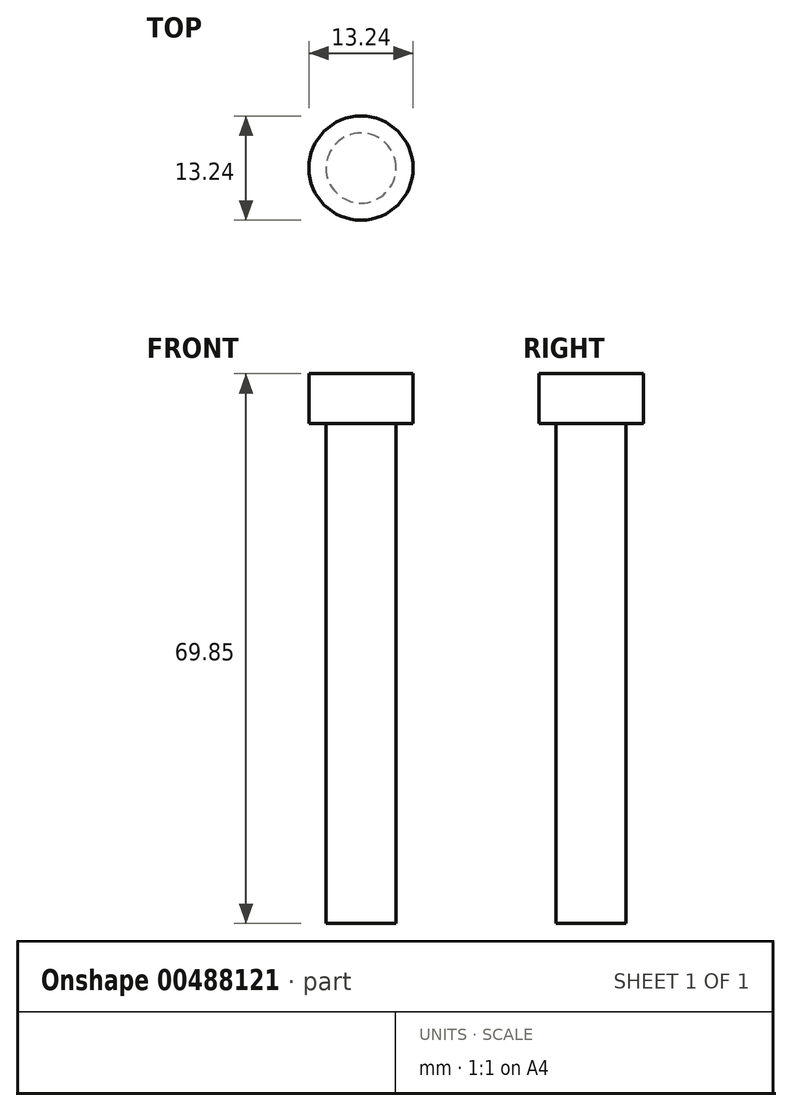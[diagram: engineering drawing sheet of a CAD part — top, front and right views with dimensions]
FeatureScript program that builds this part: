
annotation { "Feature Type Name" : "Feature", "Feature Type Description" : "" }
export const myFeature = defineFeature(function(context is Context, id is Id, definition is map)
    precondition{}
    {
        {
            var Q0;
            Q0=qCreatedBy(makeId("Top.planeOp"),FACE);
            var sketch = newSketch(context, id + "F0", { "sketchPlane" : qUnion([Q0])});
            skCircle(sketch, "E0", {"center": v(0, 0) * mm, "radius": 4.45 * mm});
            skCircle(sketch, "E1", {"center": v(0, 0) * mm, "radius": 6.62 * mm});
            skSolve(sketch);
        }
        {
            var Q0;
            Q0=makeQuery(id+"F0.imprint","IMPRINT",FACE,{"disambiguationData":[TD([[makeQuery(id+"F0.imprint","IMPRINT",EDGE,{"derivedFrom":sQuery(id+"F0.wireOp",EDGE,"E0")}),1.0]])]});
            extrude(context, id + "F1", {"entities" : qUnion([Q0]), "oppositeDirection" : true, "depth" : 63.5 * mm, "offsetDistance" : 25.4 * mm});
        }
        {
            var Q0;
            Q0=makeQuery(id+"F0.imprint","IMPRINT",FACE,{"disambiguationData":[TD([[makeQuery(id+"F0.imprint","IMPRINT",EDGE,{"derivedFrom":sQuery(id+"F0.wireOp",EDGE,"E0")}),1.0]])]});
            var Q1;
            Q1=makeQuery(id+"F0.imprint","IMPRINT",FACE,{"disambiguationData":[TD([[makeQuery(id+"F0.imprint","IMPRINT",EDGE,{"derivedFrom":sQuery(id+"F0.wireOp",EDGE,"E0")}),-1.0]])]});
            extrude(context, id + "F2", {"entities" : qUnion([Q0, Q1]), "operationType" : NewBodyOperationType.ADD, "depth" : 6.35 * mm, "offsetDistance" : 25.4 * mm});
        }
    });
